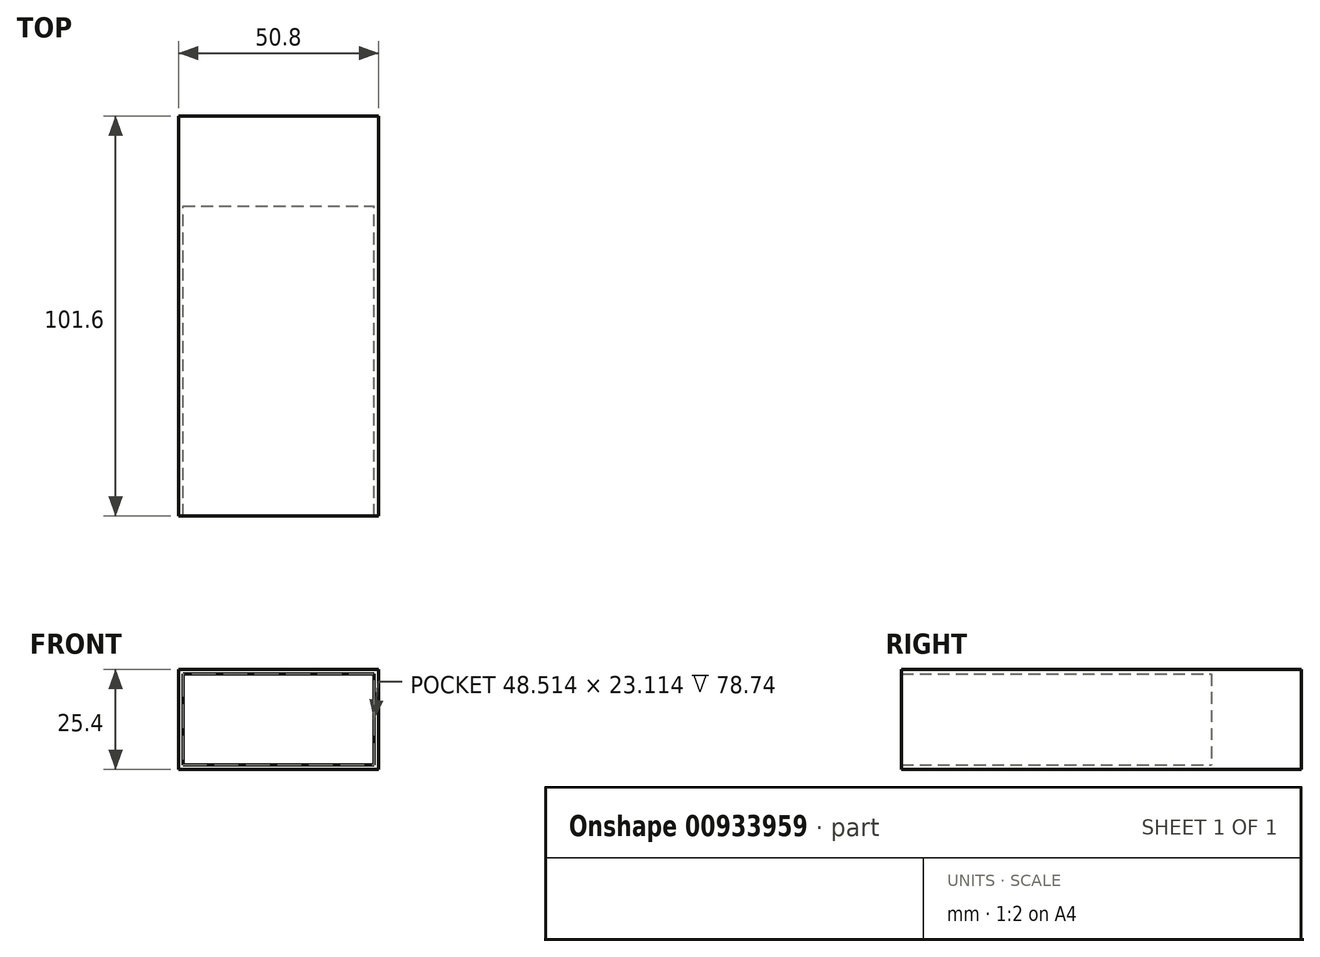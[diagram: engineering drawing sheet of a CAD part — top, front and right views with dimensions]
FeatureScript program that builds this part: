
annotation { "Feature Type Name" : "Feature", "Feature Type Description" : "" }
export const myFeature = defineFeature(function(context is Context, id is Id, definition is map)
    precondition{}
    {
        {
            var Q0;
            Q0=qCreatedBy(makeId("Front.planeOp"),FACE);
            var sketch = newSketch(context, id + "F0", { "sketchPlane" : qUnion([Q0])});
            skLineSegment(sketch, "E0.bottom", {"start": v(-25.4, 12.7) * mm, "end": v(25.4, 12.7) * mm});
            skLineSegment(sketch, "E0.top", {"start": v(-25.4, -12.7) * mm, "end": v(25.4, -12.7) * mm});
            skLineSegment(sketch, "E0.left", {"start": v(-25.4, 12.7) * mm, "end": v(-25.4, -12.7) * mm});
            skLineSegment(sketch, "E0.right", {"start": v(25.4, 12.7) * mm, "end": v(25.4, -12.7) * mm});
            skPoint(sketch, "E0.middle", {"position": v(0, 0) * mm});
            skSolve(sketch);
        }
        {
            var Q0;
            Q0=makeQuery(id+"F0.imprint","IMPRINT",FACE,{"disambiguationData":[TD([[makeQuery(id+"F0.imprint","IMPRINT",EDGE,{"derivedFrom":sQuery(id+"F0.wireOp",EDGE,"E0.bottom")}),-1.0]])]});
            var sketch = newSketch(context, id + "F1", { "sketchPlane" : qUnion([Q0])});
            skLineSegment(sketch, "E1.bottom", {"start": v(-24.26, 11.56) * mm, "end": v(24.26, 11.56) * mm});
            skLineSegment(sketch, "E1.top", {"start": v(-24.26, -11.56) * mm, "end": v(24.26, -11.56) * mm});
            skLineSegment(sketch, "E1.left", {"start": v(-24.26, 11.56) * mm, "end": v(-24.26, -11.56) * mm});
            skLineSegment(sketch, "E1.right", {"start": v(24.26, 11.56) * mm, "end": v(24.26, -11.56) * mm});
            skPoint(sketch, "E1.middle", {"position": v(0, 0) * mm});
            skSolve(sketch);
        }
        {
            var Q0;
            Q0=makeQuery(id+"F1.imprint","IMPRINT",FACE,{"disambiguationData":[TD([[makeQuery(id+"F1.imprint","IMPRINT",EDGE,{"derivedFrom":sQuery(id+"F1.wireOp",EDGE,"E1.bottom")}),1.0]])]});
            extrude(context, id + "F2", {"entities" : qUnion([Q0]), "depth" : 101.6 * mm, "offsetDistance" : 25.4 * mm});
        }
        {
            var Q0;
            Q0=qCreatedBy(makeId("Front.planeOp"),FACE);
            var sketch = newSketch(context, id + "F3", { "sketchPlane" : qUnion([Q0])});
            skLineSegment(sketch, "E2.bottom", {"start": v(-25.4, -12.7) * mm, "end": v(25.4, -12.7) * mm});
            skLineSegment(sketch, "E2.top", {"start": v(-25.4, 12.7) * mm, "end": v(25.4, 12.7) * mm});
            skLineSegment(sketch, "E2.left", {"start": v(-25.4, -12.7) * mm, "end": v(-25.4, 12.7) * mm});
            skLineSegment(sketch, "E2.right", {"start": v(25.4, -12.7) * mm, "end": v(25.4, 12.7) * mm});
            skPoint(sketch, "E2.middle", {"position": v(0, 0) * mm});
            skSolve(sketch);
        }
        {
            var Q0;
            Q0 = qSketchRegion(id + "F3", true);
            extrude(context, id + "F4", {"entities" : qUnion([Q0]), "operationType" : NewBodyOperationType.ADD, "depth" : 22.86 * mm, "offsetDistance" : 25.4 * mm});
        }
    });
